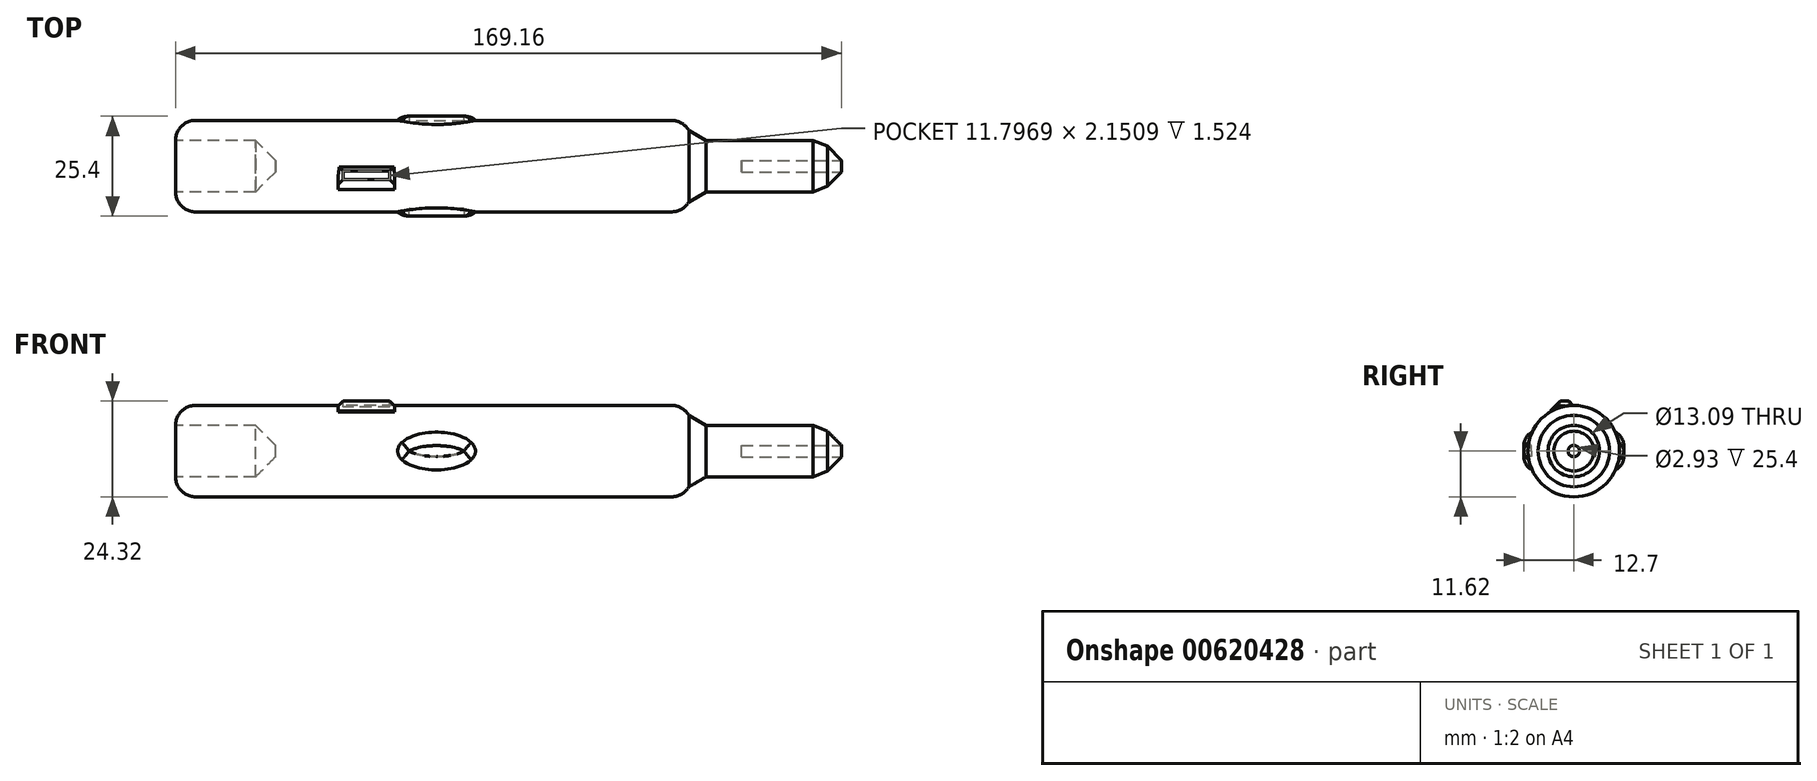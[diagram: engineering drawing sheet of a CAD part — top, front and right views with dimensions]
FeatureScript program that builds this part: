
annotation { "Feature Type Name" : "Feature", "Feature Type Description" : "" }
export const myFeature = defineFeature(function(context is Context, id is Id, definition is map)
    precondition{}
    {
        {
            var Q0;
            Q0=qCreatedBy(makeId("Right.planeOp"),FACE);
            var sketch = newSketch(context, id + "F0", { "sketchPlane" : qUnion([Q0])});
            skCircle(sketch, "E0", {"center": v(0, 0) * mm, "radius": 11.62 * mm});
            skSolve(sketch);
        }
        {
            var Q0;
            Q0 = qSketchRegion(id + "F0", true);
            extrude(context, id + "F1", {"entities" : qUnion([Q0]), "depth" : 64.77 * mm, "offsetDistance" : 25.4 * mm, "hasSecondDirection" : true, "secondDirectionOppositeDirection" : true, "secondDirectionDepth" : 66.3 * mm});
        }
        {
            var Q0;
            Q0=makeQuery(id+"F1.opExtrude","CAP_EDGE",EDGE,{"disambiguationData":[OSD([sQuery(id+"F0.wireOp",EDGE,"E0")])],"isStart":false});
            fillet(context, id + "F2", {"entities" : qUnion([Q0]), "radius" : 5.08 * mm, "tangentPropagation" : true, "allowEdgeOverflow" : false});
        }
        {
            var Q0;
            Q0=makeQuery(id+"F1.opExtrude","CAP_EDGE",EDGE,{"disambiguationData":[OSD([sQuery(id+"F0.wireOp",EDGE,"E0")])],"isStart":true});
            fillet(context, id + "F3", {"entities" : qUnion([Q0]), "radius" : 5.08 * mm, "tangentPropagation" : true, "allowEdgeOverflow" : false});
        }
        {
            var Q0;
            Q0=makeQuery(id+"F1.opExtrude","CAP_FACE",FACE,{"disambiguationData":[OSD([sQuery(id+"F0.wireOp",EDGE,"E0")])],"isStart":true});
            extrude(context, id + "F4", {"entities" : qUnion([Q0]), "operationType" : NewBodyOperationType.REMOVE, "oppositeDirection" : true, "depth" : 25.4 * mm, "offsetDistance" : 25.4 * mm});
        }
        {
            var Q0;
            Q0=makeQuery(id+"F1.opExtrude","CAP_FACE",FACE,{"disambiguationData":[OSD([sQuery(id+"F0.wireOp",EDGE,"E0")])],"isStart":false});
            extrude(context, id + "F5", {"entities" : qUnion([Q0]), "operationType" : NewBodyOperationType.REMOVE, "oppositeDirection" : true, "depth" : 25.4 * mm, "offsetDistance" : 25.4 * mm});
        }
        {
            var Q0;
            Q0=qCreatedBy(makeId("Top.planeOp"),FACE);
            var sketch = newSketch(context, id + "F6", { "sketchPlane" : qUnion([Q0])});
            skLineSegment(sketch, "E1.bottom", {"start": v(-24.95, 0) * mm, "end": v(-10.62, 0) * mm});
            skLineSegment(sketch, "E1.top", {"start": v(-24.95, -5.96) * mm, "end": v(-10.62, -5.96) * mm});
            skLineSegment(sketch, "E1.left", {"start": v(-24.95, 0) * mm, "end": v(-24.95, -5.96) * mm});
            skLineSegment(sketch, "E1.right", {"start": v(-10.62, 0) * mm, "end": v(-10.62, -5.96) * mm});
            skLineSegment(sketch, "E2", {"start": v(-22.93, 0) * mm, "end": v(-22.93, -5.96) * mm});
            skLineSegment(sketch, "E3", {"start": v(-20.95, 0) * mm, "end": v(-20.95, -5.96) * mm});
            skLineSegment(sketch, "E4", {"start": v(-21.96, 0) * mm, "end": v(-21.96, -5.96) * mm});
            skLineSegment(sketch, "E5", {"start": v(-24.61, 0) * mm, "end": v(-24.61, -5.96) * mm});
            skLineSegment(sketch, "E6", {"start": v(-24.1, 0) * mm, "end": v(-24.1, -5.96) * mm});
            skLineSegment(sketch, "E7", {"start": v(-23.66, 0) * mm, "end": v(-23.66, -5.96) * mm});
            skLineSegment(sketch, "E8", {"start": v(-21.44, 0) * mm, "end": v(-21.44, -5.96) * mm});
            skLineSegment(sketch, "E9", {"start": v(-22.42, 0) * mm, "end": v(-22.42, -5.96) * mm});
            skLineSegment(sketch, "E10", {"start": v(-23.44, 0) * mm, "end": v(-23.44, -5.96) * mm});
            skLineSegment(sketch, "E11", {"start": v(-20.55, -5.96) * mm, "end": v(-20.55, 0) * mm});
            skLineSegment(sketch, "E12", {"start": v(-20, 0) * mm, "end": v(-20, -5.96) * mm});
            skLineSegment(sketch, "E13", {"start": v(-19.68, -5.96) * mm, "end": v(-19.68, 0) * mm});
            skLineSegment(sketch, "E14", {"start": v(-19.1, 0.11) * mm, "end": v(-19.1, -5.96) * mm});
            skLineSegment(sketch, "E15", {"start": v(-18.64, 0) * mm, "end": v(-18.64, -5.96) * mm});
            skLineSegment(sketch, "E16", {"start": v(-18.25, 0) * mm, "end": v(-18.25, -5.96) * mm});
            skLineSegment(sketch, "E17", {"start": v(-17.43, 0) * mm, "end": v(-17.43, -5.96) * mm});
            skLineSegment(sketch, "E18", {"start": v(-17.43, -5.96) * mm, "end": v(-17.43, 0) * mm});
            skLineSegment(sketch, "E19", {"start": v(-17.78, 0) * mm, "end": v(-17.78, -5.96) * mm});
            skLineSegment(sketch, "E20", {"start": v(-17.16, -5.96) * mm, "end": v(-17.16, 0.11) * mm});
            skLineSegment(sketch, "E21", {"start": v(-16.82, 0) * mm, "end": v(-16.82, -5.96) * mm});
            skLineSegment(sketch, "E22", {"start": v(-16.29, -5.96) * mm, "end": v(-16.29, 0) * mm});
            skLineSegment(sketch, "E23", {"start": v(-15.85, 0) * mm, "end": v(-15.85, -5.96) * mm});
            skLineSegment(sketch, "E24", {"start": v(-15.54, 0) * mm, "end": v(-15.54, -5.96) * mm});
            skLineSegment(sketch, "E25", {"start": v(-15.22, -5.96) * mm, "end": v(-15.22, 0) * mm});
            skLineSegment(sketch, "E26", {"start": v(-15.22, 0) * mm, "end": v(-15.22, -5.96) * mm});
            skLineSegment(sketch, "E27", {"start": v(-14.79, -5.96) * mm, "end": v(-14.79, 0) * mm});
            skLineSegment(sketch, "E28", {"start": v(-14.33, 0) * mm, "end": v(-14.33, -5.96) * mm});
            skLineSegment(sketch, "E29", {"start": v(-13.76, -5.96) * mm, "end": v(-13.76, 0) * mm});
            skLineSegment(sketch, "E30", {"start": v(-13.32, -5.96) * mm, "end": v(-13.32, 0) * mm});
            skLineSegment(sketch, "E31", {"start": v(-12.76, 0) * mm, "end": v(-12.76, -5.96) * mm});
            skLineSegment(sketch, "E32", {"start": v(-12.2, -5.93) * mm, "end": v(-12.2, 0) * mm});
            skLineSegment(sketch, "E33", {"start": v(-11.75, 0) * mm, "end": v(-11.75, -5.96) * mm});
            skLineSegment(sketch, "E34", {"start": v(-11.23, -5.96) * mm, "end": v(-11.23, 0) * mm});
            skSolve(sketch);
        }
        {
            var Q0;
            Q0 = qSketchRegion(id + "F6", true);
            extrude(context, id + "F7", {"entities" : qUnion([Q0]), "operationType" : NewBodyOperationType.ADD, "depth" : 12.7 * mm, "offsetDistance" : 25.4 * mm});
        }
        {
            var Q0;
            Q0=makeQuery(id+"F7.opExtrude","CAP_EDGE",EDGE,{"disambiguationData":[OSD([sQuery(id+"F6.wireOp",EDGE,"E1.top")])],"isStart":false});
            chamfer(context, id + "F8", {"entities" : qUnion([Q0]), "width" : 2.54 * mm, "tangentPropagation" : true});
        }
        {
            var Q0;
            Q0=makeQuery(id+"F7.opExtrude","CAP_EDGE",EDGE,{"disambiguationData":[OSD([sQuery(id+"F6.wireOp",EDGE,"E1.bottom")])],"isStart":false});
            chamfer(context, id + "F9", {"entities" : qUnion([Q0]), "width" : 1.27 * mm, "tangentPropagation" : true});
        }
        {
            var Q0;
            Q0=makeQuery(id+"F7.opExtrude","CAP_EDGE",EDGE,{"disambiguationData":[OSD([sQuery(id+"F6.wireOp",EDGE,"E1.left")])],"isStart":false});
            var Q1;
            Q1=makeQuery(id+"F7.opExtrude","CAP_EDGE",EDGE,{"disambiguationData":[OSD([sQuery(id+"F6.wireOp",EDGE,"E1.right")])],"isStart":false});
            chamfer(context, id + "F10", {"entities" : qUnion([Q0, Q1]), "width" : 1.27 * mm, "tangentPropagation" : true});
        }
        {
            var Q0;
            Q0=qCreatedBy(makeId("Front.planeOp"),FACE);
            var sketch = newSketch(context, id + "F11", { "sketchPlane" : qUnion([Q0])});
            skEllipse(sketch, "E35", {"center": v(0, 0) * mm, "majorRadius": 9.88 * mm, "minorRadius": 4.8 * mm, "majorAxis": v(1, 0)});
            skSolve(sketch);
        }
        {
            var Q0;
            Q0 = qSketchRegion(id + "F11", true);
            extrude(context, id + "F12", {"entities" : qUnion([Q0]), "operationType" : NewBodyOperationType.ADD, "depth" : 12.7 * mm, "offsetDistance" : 25.4 * mm, "hasSecondDirection" : true, "secondDirectionOppositeDirection" : true, "secondDirectionDepth" : 12.7 * mm});
        }
        {
            var Q0;
            Q0=makeQuery(id+"F12.opExtrude","CAP_EDGE",EDGE,{"disambiguationData":[OSD([sQuery(id+"F11.wireOp",EDGE,"E35")])],"isStart":true});
            var Q1;
            Q1=makeQuery(id+"F12.opExtrude","CAP_EDGE",EDGE,{"disambiguationData":[OSD([sQuery(id+"F11.wireOp",EDGE,"E35")])],"isStart":false});
            fillet(context, id + "F13", {"entities" : qUnion([Q0, Q1]), "radius" : 3.8 * mm, "tangentPropagation" : true, "allowEdgeOverflow" : false});
        }
        {
            var Q0;
            Q0=makeQuery(id+"F12.opExtrude","CAP_FACE",FACE,{"disambiguationData":[OSD([sQuery(id+"F11.wireOp",EDGE,"E35")])],"isStart":false});
            var Q1;
            Q1=makeQuery(id+"F12.opExtrude","CAP_FACE",FACE,{"disambiguationData":[OSD([sQuery(id+"F11.wireOp",EDGE,"E35")])],"isStart":true});
            extrude(context, id + "F14", {"entities" : qUnion([Q0, Q1]), "operationType" : NewBodyOperationType.REMOVE, "oppositeDirection" : true, "depth" : 1.9 * mm, "offsetDistance" : 25.4 * mm});
        }
        {
            var Q0;
            Q0=makeQuery(id+"F12.opExtrude","CAP_FACE",FACE,{"disambiguationData":[OSD([sQuery(id+"F11.wireOp",EDGE,"E35")])],"isStart":true});
            extrude(context, id + "F15", {"entities" : qUnion([Q0]), "operationType" : NewBodyOperationType.REMOVE, "oppositeDirection" : true, "depth" : 1.27 * mm, "offsetDistance" : 25.4 * mm});
        }
        {
            var Q0;
            Q0 = qSketchRegion(id + "F6", true);
            extrude(context, id + "F16", {"entities" : qUnion([Q0]), "operationType" : NewBodyOperationType.ADD, "depth" : 2.54 * mm, "offsetDistance" : 25.4 * mm});
        }
        {
            var Q0;
            Q0=makeQuery(id+"F7.opExtrude","CAP_FACE",FACE,{"disambiguationData":[OSD([sQuery(id+"F6.wireOp",EDGE,"E1.bottom"),sQuery(id+"F6.wireOp",EDGE,"E1.top"),sQuery(id+"F6.wireOp",EDGE,"E1.left"),sQuery(id+"F6.wireOp",EDGE,"E1.right")])],"isStart":false});
            extrude(context, id + "F17", {"entities" : qUnion([Q0]), "operationType" : NewBodyOperationType.REMOVE, "oppositeDirection" : true, "depth" : 1.52 * mm, "offsetDistance" : 25.4 * mm});
        }
        {
            var Q0;
            Q0=makeQuery(id+"F5.boolean.opBoolean","COPY",FACE,{"derivedFrom":makeQuery(id+"F5.opExtrude","CAP_FACE",FACE,{"disambiguationData":[OSD([sQuery(id+"F0.wireOp",EDGE,"E0")])],"isStart":false})});
            extrude(context, id + "F18", {"entities" : qUnion([Q0]), "operationType" : NewBodyOperationType.ADD, "depth" : 63.5 * mm, "offsetDistance" : 25.4 * mm});
        }
        {
            var Q0;
            Q0=makeQuery(id+"F18.opExtrude","CAP_EDGE",EDGE,{"disambiguationData":[OSD([sQuery(id+"F0.wireOp",EDGE,"E0")])],"isStart":false});
            chamfer(context, id + "F19", {"entities" : qUnion([Q0]), "width" : 5.08 * mm, "tangentPropagation" : true});
        }
        {
            var Q0;
            Q0=makeQuery(id+"F18.opExtrude","CAP_FACE",FACE,{"disambiguationData":[OSD([sQuery(id+"F0.wireOp",EDGE,"E0")])],"isStart":false});
            extrude(context, id + "F20", {"entities" : qUnion([Q0]), "operationType" : NewBodyOperationType.REMOVE, "oppositeDirection" : true, "depth" : 25.4 * mm, "offsetDistance" : 25.4 * mm});
        }
        {
            var Q0;
            Q0=makeQuery(id+"F18.opExtrude","SWEPT_FACE",FACE,{"disambiguationData":[OSD([sQuery(id+"F0.wireOp",EDGE,"E0")])]});
            chamfer(context, id + "F21", {"entities" : qUnion([Q0]), "width" : 5.08 * mm, "tangentPropagation" : true});
        }
        {
            var Q0;
            Q0=makeQuery(id+"F4.boolean.opBoolean","COPY",FACE,{"derivedFrom":makeQuery(id+"F4.opExtrude","CAP_FACE",FACE,{"disambiguationData":[OSD([sQuery(id+"F0.wireOp",EDGE,"E0")])],"isStart":false})});
            chamfer(context, id + "F22", {"entities" : qUnion([Q0]), "width" : 5.08 * mm, "tangentPropagation" : true});
        }
    });
